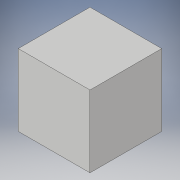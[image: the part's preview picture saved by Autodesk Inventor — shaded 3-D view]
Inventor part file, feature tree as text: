
AUTODESK INVENTOR PART (.ipt)
format: ipt  version: 2017 (Build 210142000, 142)  size: 83,456 bytes
history: native  units: mm
features: extrude x1, sketch x1
ambient origin geometry x8: Origin, YZ Plane, XZ Plane, XY Plane, X Axis, Y Axis, Z Axis, Center Point
bodies: Volumenkörper1 (feature_tree)
feature tree (2):
  extrude  "Extrusion1"  Depth=10.0mm
  sketch  "Skizze1"  dims[d0=10.0mm d1=10.0mm d2=10.0mm d3=0.0mm]
